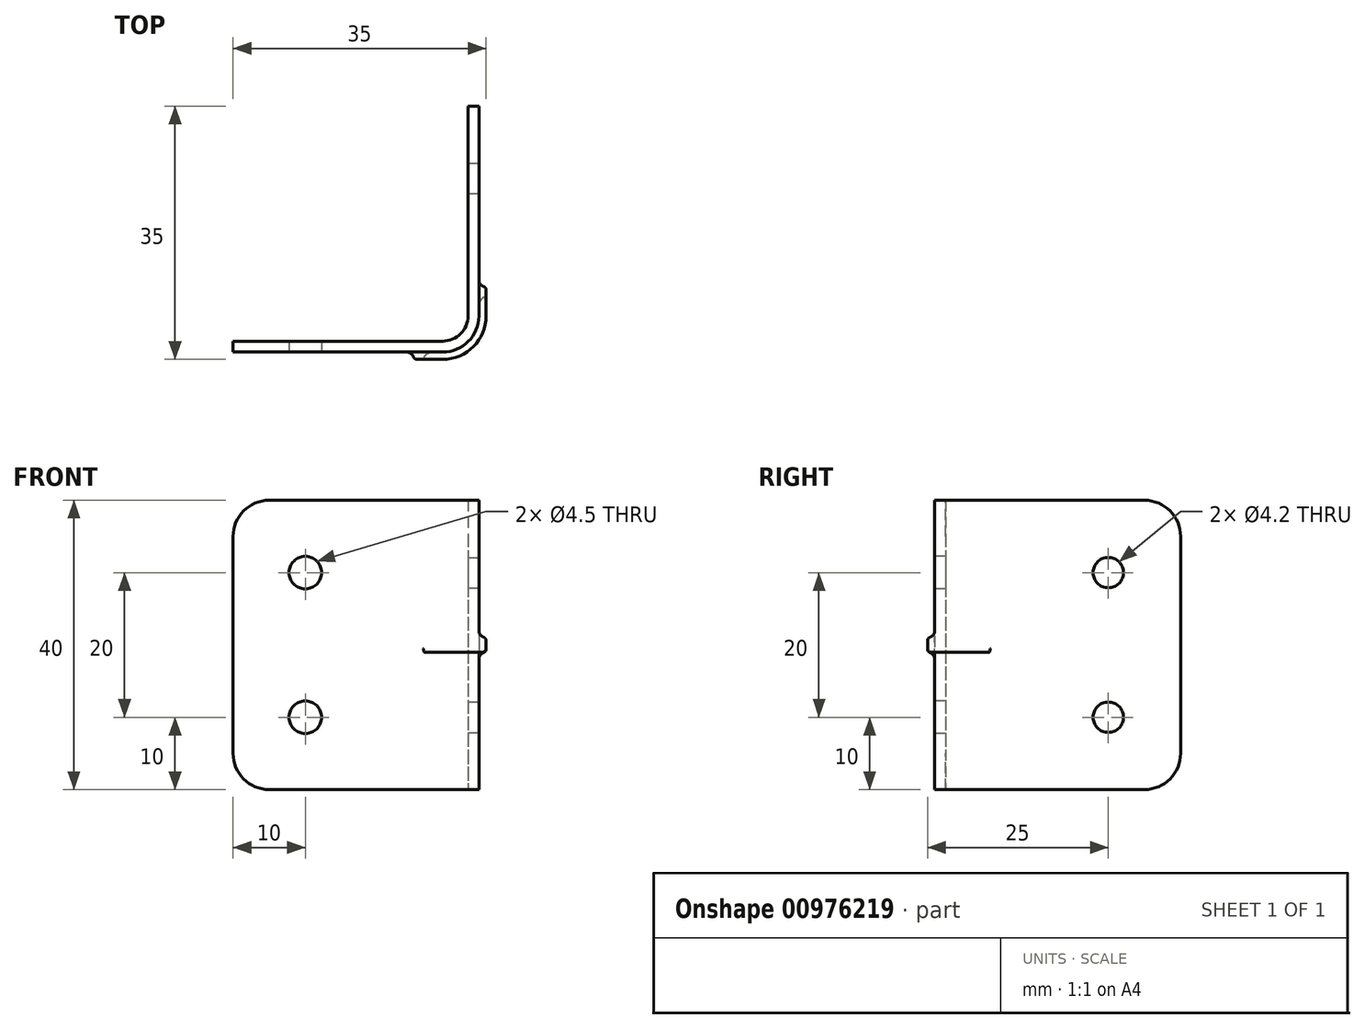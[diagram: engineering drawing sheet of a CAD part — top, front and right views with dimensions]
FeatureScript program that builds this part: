
annotation { "Feature Type Name" : "Feature", "Feature Type Description" : "" }
export const myFeature = defineFeature(function(context is Context, id is Id, definition is map)
    precondition{}
    {
        {
            var Q0;
            Q0=qCreatedBy(makeId("Top.planeOp"),FACE);
            var sketch = newSketch(context, id + "F0", { "sketchPlane" : qUnion([Q0])});
            skLineSegment(sketch, "E0", {"start": v(-34, 0) * mm, "end": v(-5, 0) * mm});
            skLineSegment(sketch, "E1", {"start": v(0, 5) * mm, "end": v(0, 34) * mm});
            skPoint(sketch, "E2.visualSharp", {"position": v(0, 0) * mm});
            skArc(sketch, "E2.filletArc", {"start": v(-5, 0) * mm, "mid": v(-1.46, 1.46) * mm, "end": v(0, 5) * mm});
            skLineSegment(sketch, "E3.0", {"start": v(-1.5, 5) * mm, "end": v(-1.5, 34) * mm});
            skArc(sketch, "E3.1", {"start": v(-5, 1.5) * mm, "mid": v(-2.53, 2.53) * mm, "end": v(-1.5, 5) * mm});
            skLineSegment(sketch, "E3.2", {"start": v(-34, 1.5) * mm, "end": v(-5, 1.5) * mm});
            skLineSegment(sketch, "E4", {"start": v(-34, 1.5) * mm, "end": v(-34, 0) * mm});
            skLineSegment(sketch, "E5", {"start": v(-1.5, 34) * mm, "end": v(0, 34) * mm});
            skSolve(sketch);
        }
        {
            var Q0;
            Q0 = qSketchRegion(id + "F0", true);
            extrude(context, id + "F1", {"entities" : qUnion([Q0]), "endBound" : BoundingType.SYMMETRIC, "depth" : 40 * mm, "offsetDistance" : 25 * mm});
        }
        {
            var Q0;
            Q0=makeQuery(id+"F1.opExtrude","CAP_EDGE",EDGE,{"disambiguationData":[OSD([sQuery(id+"F0.wireOp",EDGE,"E4")])],"isStart":false});
            var Q1;
            Q1=makeQuery(id+"F1.opExtrude","CAP_EDGE",EDGE,{"disambiguationData":[OSD([sQuery(id+"F0.wireOp",EDGE,"E4")])],"isStart":true});
            var Q2;
            Q2=makeQuery(id+"F1.opExtrude","CAP_EDGE",EDGE,{"disambiguationData":[OSD([sQuery(id+"F0.wireOp",EDGE,"E5")])],"isStart":true});
            var Q3;
            Q3=makeQuery(id+"F1.opExtrude","CAP_EDGE",EDGE,{"disambiguationData":[OSD([sQuery(id+"F0.wireOp",EDGE,"E5")])],"isStart":false});
            fillet(context, id + "F2", {"entities" : qUnion([Q0, Q1, Q2, Q3]), "radius" : 5 * mm, "tangentPropagation" : true, "allowEdgeOverflow" : false});
        }
        {
            var Q0;
            Q0=makeQuery(id+"F1.opExtrude","SWEPT_FACE",FACE,{"disambiguationData":[OSD([sQuery(id+"F0.wireOp",EDGE,"E0")])]});
            var sketch = newSketch(context, id + "F3", { "sketchPlane" : qUnion([Q0])});
            skLineSegment(sketch, "E6", {"start": v(0, 0) * mm, "end": v(-34, 0) * mm, "construction": true});
            skPoint(sketch, "E6.endSnap0", {"position": v(-34, 0) * mm});
            skCircle(sketch, "E7", {"center": v(-24, 10) * mm, "radius": 2.25 * mm});
            skCircle(sketch, "E8.MirrorC", {"center": v(-24, -10) * mm, "radius": 2.25 * mm});
            skSolve(sketch);
        }
        {
            var Q0;
            Q0 = qSketchRegion(id + "F3", true);
            extrude(context, id + "F4", {"entities" : qUnion([Q0]), "operationType" : NewBodyOperationType.REMOVE, "endBound" : BoundingType.THROUGH_ALL, "oppositeDirection" : true, "depth" : 25 * mm, "offsetDistance" : 25 * mm});
        }
        {
            var Q0;
            Q0=makeQuery(id+"F1.opExtrude","SWEPT_FACE",FACE,{"disambiguationData":[OSD([sQuery(id+"F0.wireOp",EDGE,"E1")])]});
            var sketch = newSketch(context, id + "F5", { "sketchPlane" : qUnion([Q0])});
            skLineSegment(sketch, "E9", {"start": v(0, 0) * mm, "end": v(34, 0) * mm, "construction": true});
            skCircle(sketch, "E10", {"center": v(24, 10) * mm, "radius": 2.1 * mm});
            skCircle(sketch, "E11.MirrorC", {"center": v(24, -10) * mm, "radius": 2.1 * mm});
            skSolve(sketch);
        }
        {
            var Q0;
            Q0 = qSketchRegion(id + "F5", true);
            extrude(context, id + "F6", {"entities" : qUnion([Q0]), "operationType" : NewBodyOperationType.REMOVE, "surfaceOperationType" : NewSurfaceOperationType.ADD, "endBound" : BoundingType.THROUGH_ALL, "oppositeDirection" : true, "depth" : 25 * mm, "offsetDistance" : 25 * mm});
        }
        {
            var Q0;
            Q0=qCreatedBy(makeId("Top.planeOp"),FACE);
            var sketch = newSketch(context, id + "F7", { "sketchPlane" : qUnion([Q0])});
            skLineSegment(sketch, "E12.0", {"start": v(1, 5) * mm, "end": v(1, 9) * mm});
            skArc(sketch, "E12.1", {"start": v(-5, -1) * mm, "mid": v(-0.76, 0.76) * mm, "end": v(1, 5) * mm});
            skLineSegment(sketch, "E12.2", {"start": v(-9, -1) * mm, "end": v(-5, -1) * mm});
            skLineSegment(sketch, "E13", {"start": v(-9, -1) * mm, "end": v(-9, 0.68) * mm, "construction": true});
            skLineSegment(sketch, "E14", {"start": v(-9, 0.68) * mm, "end": v(-0.68, 9) * mm, "construction": true});
            skLineSegment(sketch, "E15", {"start": v(-0.68, 9) * mm, "end": v(1, 9) * mm, "construction": true});
            skLineSegment(sketch, "E16.0", {"start": v(-0.5, 5) * mm, "end": v(-0.5, 9) * mm});
            skArc(sketch, "E16.1", {"start": v(-5, 0.5) * mm, "mid": v(-1.82, 1.82) * mm, "end": v(-0.5, 5) * mm});
            skLineSegment(sketch, "E16.2", {"start": v(-9, 0.5) * mm, "end": v(-5, 0.5) * mm});
            skLineSegment(sketch, "E17", {"start": v(-9, -1) * mm, "end": v(-9, 0.5) * mm});
            skLineSegment(sketch, "E18", {"start": v(-0.5, 9) * mm, "end": v(1, 9) * mm});
            skSolve(sketch);
        }
        {
            var Q0;
            Q0 = qSketchRegion(id + "F7", true);
            extrude(context, id + "F8", {"entities" : qUnion([Q0]), "operationType" : NewBodyOperationType.ADD, "endBound" : BoundingType.SYMMETRIC, "depth" : 2 * mm, "offsetDistance" : 25 * mm});
        }
        {
            var Q0;
            Q0=makeQuery(id+"F8.opExtrude","CAP_EDGE",EDGE,{"disambiguationData":[OSD([sQuery(id+"F7.wireOp",EDGE,"E17")])],"isStart":false});
            var Q1;
            Q1=makeQuery(id+"F8.opExtrude","CAP_EDGE",EDGE,{"disambiguationData":[OSD([sQuery(id+"F7.wireOp",EDGE,"E17")])],"isStart":true});
            var Q2;
            Q2=makeQuery(id+"F8.opExtrude","CAP_EDGE",EDGE,{"disambiguationData":[OSD([sQuery(id+"F7.wireOp",EDGE,"E18")])],"isStart":false});
            var Q3;
            Q3=makeQuery(id+"F8.opExtrude","CAP_EDGE",EDGE,{"disambiguationData":[OSD([sQuery(id+"F7.wireOp",EDGE,"E18")])],"isStart":true});
            var Q4;
            Q4=makeQuery(id+"F8.boolean.opBoolean","INTERSECT",EDGE,{"derivedFrom":[makeQuery(id+"F1.opExtrude","SWEPT_FACE",FACE,{"disambiguationData":[OSD([sQuery(id+"F0.wireOp",EDGE,"E0")])]}),makeQuery(id+"F8.opExtrude","CAP_FACE",FACE,{"disambiguationData":[OSD([sQuery(id+"F7.wireOp",EDGE,"E12.0"),sQuery(id+"F7.wireOp",EDGE,"E12.1"),sQuery(id+"F7.wireOp",EDGE,"E12.2"),sQuery(id+"F7.wireOp",EDGE,"E16.0"),sQuery(id+"F7.wireOp",EDGE,"E16.1"),sQuery(id+"F7.wireOp",EDGE,"E16.2"),sQuery(id+"F7.wireOp",EDGE,"E17"),sQuery(id+"F7.wireOp",EDGE,"E18")])],"isStart":false})]});
            fillet(context, id + "F9", {"entities" : qUnion([Q0, Q1, Q2, Q3, Q4]), "radius" : 1 * mm, "tangentPropagation" : true, "allowEdgeOverflow" : false});
        }
        {
            var Q0;
            {var subQ0=sQuery(id+"F7.wireOp",EDGE,"E12.1");Q0=makeQuery(id+"F9.opFillet","BLEND_EDGE",EDGE,{"blendedFrom":[makeQuery(id+"F8.boolean.opBoolean","INTERSECT",EDGE,{"derivedFrom":[makeQuery(id+"F1.opExtrude","SWEPT_FACE",FACE,{"disambiguationData":[OSD([sQuery(id+"F0.wireOp",EDGE,"E2.filletArc")])]}),makeQuery(id+"F8.opExtrude","CAP_FACE",FACE,{"disambiguationData":[OSD([sQuery(id+"F7.wireOp",EDGE,"E12.0"),subQ0,sQuery(id+"F7.wireOp",EDGE,"E12.2"),sQuery(id+"F7.wireOp",EDGE,"E16.0"),sQuery(id+"F7.wireOp",EDGE,"E16.1"),sQuery(id+"F7.wireOp",EDGE,"E16.2"),sQuery(id+"F7.wireOp",EDGE,"E17"),sQuery(id+"F7.wireOp",EDGE,"E18")])],"isStart":false})]}),makeQuery(id+"F8.opExtrude","SWEPT_FACE",FACE,{"disambiguationData":[OSD([subQ0])]})],"blendedInto":[makeQuery(id+"F8.opExtrude","SWEPT_FACE",FACE,{"disambiguationData":[OSD([subQ0])]})]});}
            fillet(context, id + "F10", {"entities" : qUnion([Q0]), "radius" : 0.5 * mm, "tangentPropagation" : true, "allowEdgeOverflow" : false});
        }
    });
